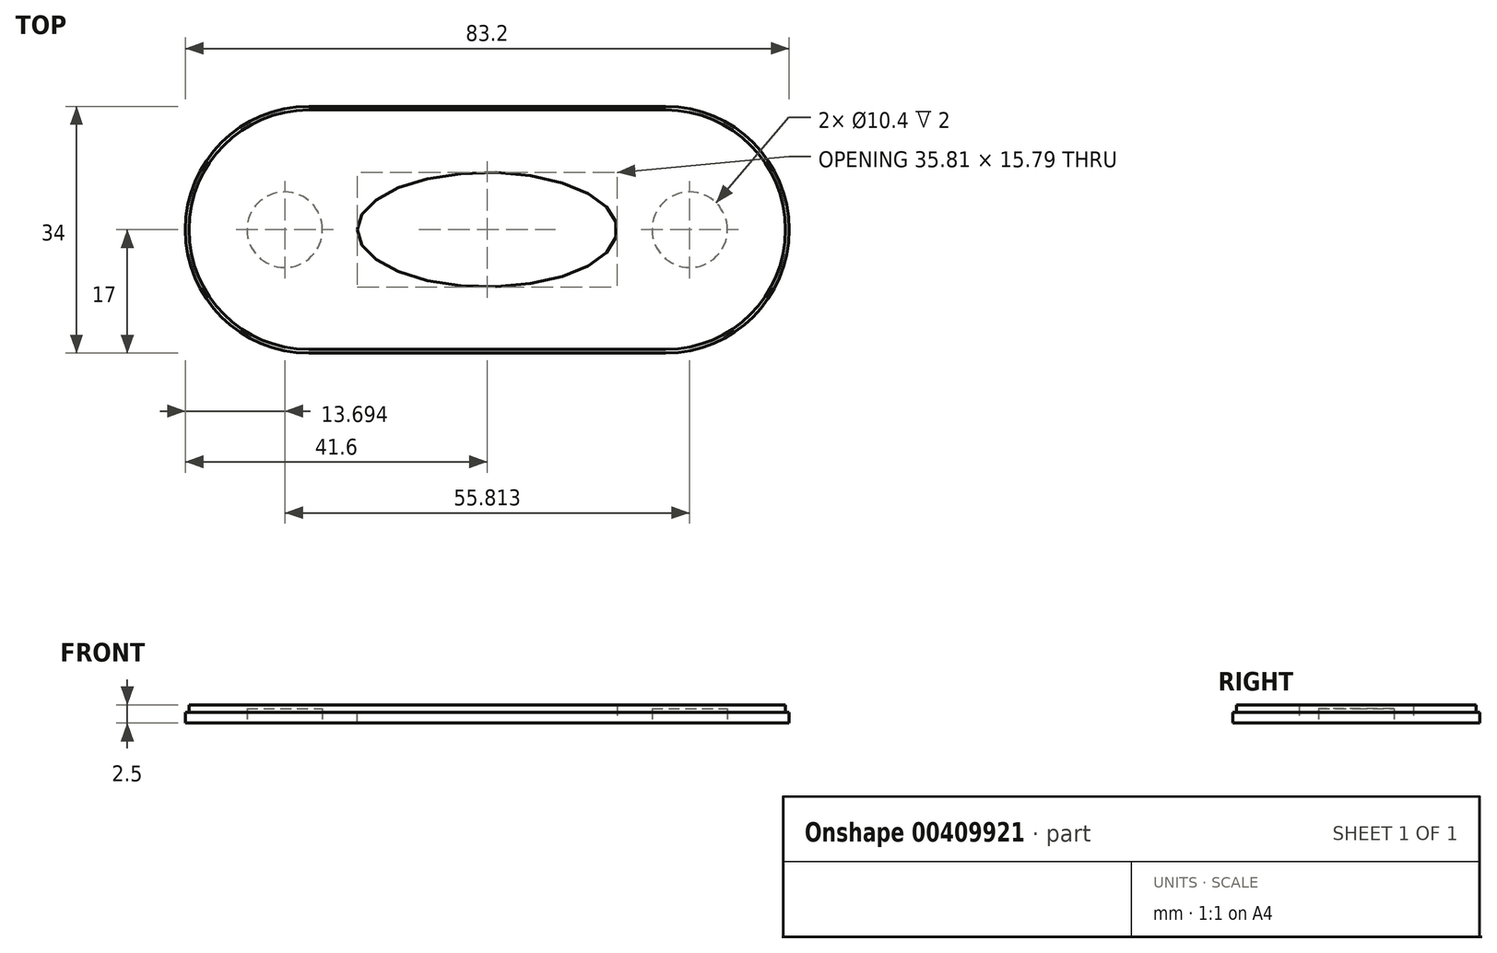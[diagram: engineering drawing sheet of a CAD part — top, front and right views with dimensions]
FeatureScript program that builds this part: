
annotation { "Feature Type Name" : "Feature", "Feature Type Description" : "" }
export const myFeature = defineFeature(function(context is Context, id is Id, definition is map)
    precondition{}
    {
        {
            var Q0;
            Q0=qCreatedBy(makeId("Top.planeOp"),FACE);
            var sketch = newSketch(context, id + "F0", { "sketchPlane" : qUnion([Q0])});
            skLineSegment(sketch, "E0.bottom", {"start": v(-24.6, 17) * mm, "end": v(24.6, 17) * mm});
            skLineSegment(sketch, "E0.top", {"start": v(-24.6, -17) * mm, "end": v(24.6, -17) * mm});
            skPoint(sketch, "E0.middle", {"position": v(0, 0) * mm});
            skArc(sketch, "E1", {"start": v(-24.6, 17) * mm, "mid": v(-41.6, 0) * mm, "end": v(-24.6, -17) * mm});
            skArc(sketch, "E2", {"start": v(24.6, -17) * mm, "mid": v(41.6, 0) * mm, "end": v(24.6, 17) * mm});
            skSolve(sketch);
        }
        {
            var Q0;
            Q0 = qSketchRegion(id + "F0", true);
            extrude(context, id + "F1", {"entities" : qUnion([Q0]), "depth" : 1.5 * mm});
        }
        {
            var Q0;
            Q0=makeQuery(id+"F1.opExtrude","CAP_FACE",FACE,{"disambiguationData":[OSD([sQuery(id+"F0.wireOp",EDGE,"E0.bottom"),sQuery(id+"F0.wireOp",EDGE,"E0.top"),sQuery(id+"F0.wireOp",EDGE,"E1"),sQuery(id+"F0.wireOp",EDGE,"E2")])],"isStart":false});
            var sketch = newSketch(context, id + "F2", { "sketchPlane" : qUnion([Q0])});
            skPoint(sketch, "E3", {"position": v(-24.6, -17) * mm});
            skPoint(sketch, "E4", {"position": v(-24.6, 17) * mm});
            skPoint(sketch, "E5", {"position": v(24.6, 17) * mm});
            skPoint(sketch, "E6", {"position": v(24.6, -17) * mm});
            skLineSegment(sketch, "E7.0", {"start": v(-24.6, 16.5) * mm, "end": v(24.6, 16.5) * mm});
            skArc(sketch, "E7.1", {"start": v(-24.6, 16.5) * mm, "mid": v(-41.1, 0) * mm, "end": v(-24.6, -16.5) * mm});
            skLineSegment(sketch, "E7.2", {"start": v(-24.6, -16.5) * mm, "end": v(24.6, -16.5) * mm});
            skArc(sketch, "E7.3", {"start": v(24.6, -16.5) * mm, "mid": v(41.1, 0) * mm, "end": v(24.6, 16.5) * mm});
            skSolve(sketch);
        }
        {
            var Q0;
            Q0 = qSketchRegion(id + "F2", true);
            extrude(context, id + "F3", {"entities" : qUnion([Q0]), "operationType" : NewBodyOperationType.ADD, "depth" : 1 * mm});
        }
        {
            var Q0;
            Q0=makeQuery(id+"F3.opExtrude","CAP_FACE",FACE,{"disambiguationData":[OSD([sQuery(id+"F2.wireOp",EDGE,"E7.0"),sQuery(id+"F2.wireOp",EDGE,"E7.1"),sQuery(id+"F2.wireOp",EDGE,"E7.2"),sQuery(id+"F2.wireOp",EDGE,"E7.3")])],"isStart":false});
            var sketch = newSketch(context, id + "F4", { "sketchPlane" : qUnion([Q0])});
            skEllipse(sketch, "E8", {"center": v(0, 0) * mm, "majorRadius": 17.9 * mm, "minorRadius": 7.9 * mm, "majorAxis": v(-1, 0)});
            skSolve(sketch);
        }
        {
            var Q0;
            Q0 = qSketchRegion(id + "F4", true);
            extrude(context, id + "F5", {"entities" : qUnion([Q0]), "operationType" : NewBodyOperationType.REMOVE, "oppositeDirection" : true, "depth" : 25 * mm});
        }
        {
            var Q0;
            Q0=makeQuery(id+"F1.opExtrude","CAP_FACE",FACE,{"disambiguationData":[OSD([sQuery(id+"F0.wireOp",EDGE,"E0.bottom"),sQuery(id+"F0.wireOp",EDGE,"E0.top"),sQuery(id+"F0.wireOp",EDGE,"E1"),sQuery(id+"F0.wireOp",EDGE,"E2")])],"isStart":true});
            var sketch = newSketch(context, id + "F6", { "sketchPlane" : qUnion([Q0])});
            skPoint(sketch, "E9", {"position": v(-17.9, 0) * mm});
            skPoint(sketch, "E10", {"position": v(-27.9, 0) * mm});
            skPoint(sketch, "E11", {"position": v(17.9, 0) * mm});
            skPoint(sketch, "E12", {"position": v(27.9, 0) * mm});
            skCircle(sketch, "E13", {"center": v(-27.9, 0) * mm, "radius": 5.2 * mm});
            skCircle(sketch, "E14", {"center": v(27.9, 0) * mm, "radius": 5.2 * mm});
            skSolve(sketch);
        }
        {
            var Q0;
            Q0 = qSketchRegion(id + "F6", true);
            extrude(context, id + "F7", {"entities" : qUnion([Q0]), "operationType" : NewBodyOperationType.REMOVE, "oppositeDirection" : true, "depth" : 2 * mm});
        }
    });
